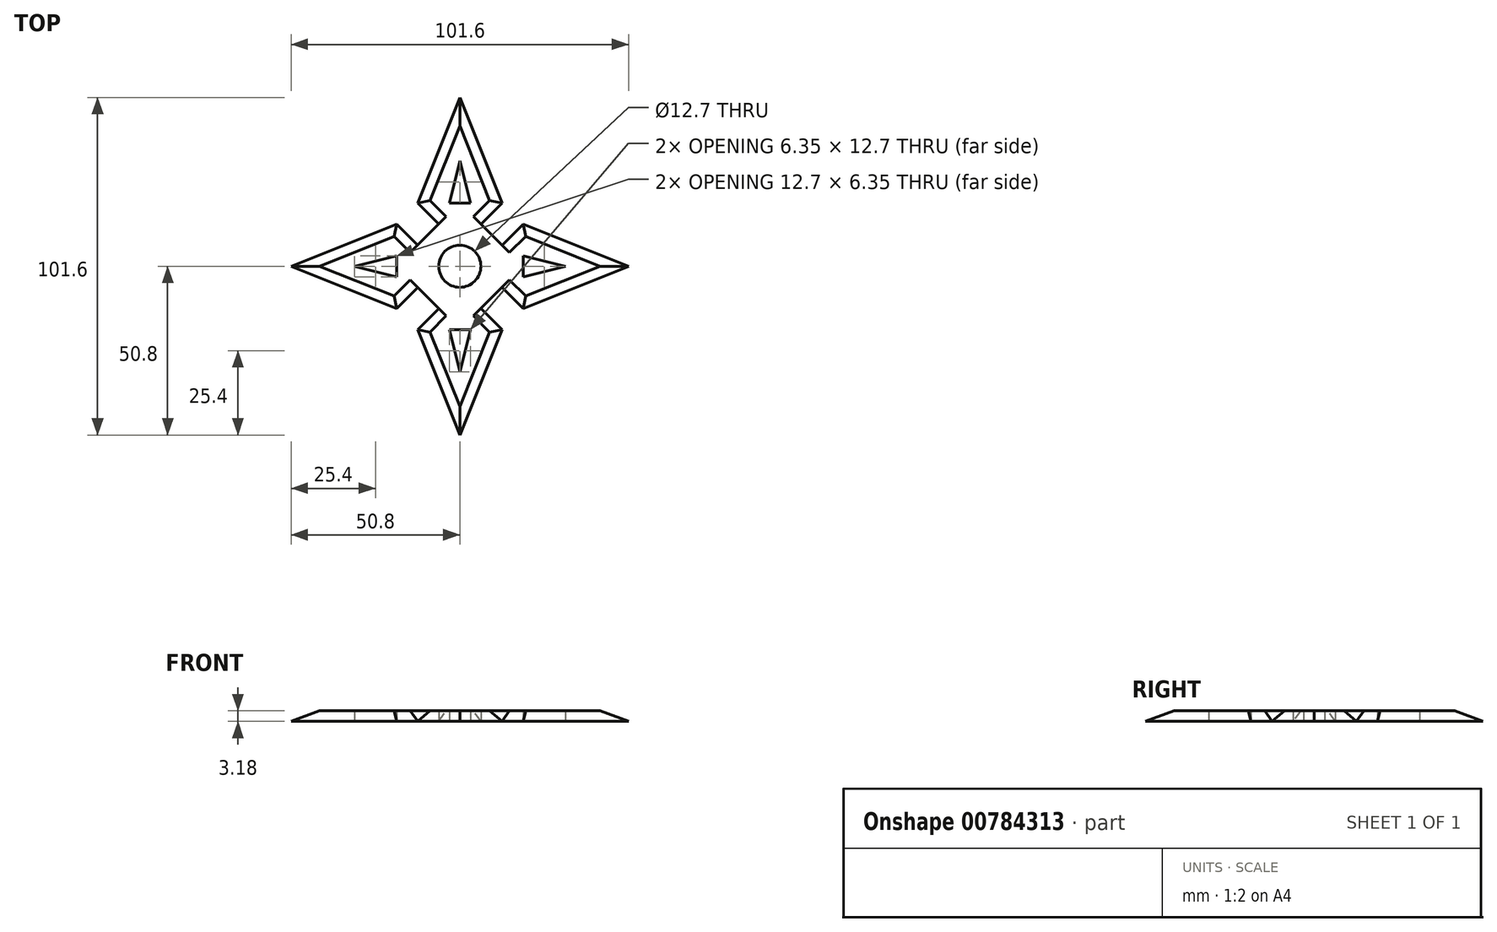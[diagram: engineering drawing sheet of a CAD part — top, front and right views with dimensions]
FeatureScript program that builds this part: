
annotation { "Feature Type Name" : "Feature", "Feature Type Description" : "" }
export const myFeature = defineFeature(function(context is Context, id is Id, definition is map)
    precondition{}
    {
        {
            var Q0;
            Q0=qCreatedBy(makeId("Top.planeOp"),FACE);
            var sketch = newSketch(context, id + "F0", { "sketchPlane" : qUnion([Q0])});
            skLineSegment(sketch, "E0", {"start": v(-12.7, 6.35) * mm, "end": v(-12.7, -6.35) * mm});
            skLineSegment(sketch, "E1", {"start": v(-12.7, -6.35) * mm, "end": v(-6.35, -12.7) * mm});
            skLineSegment(sketch, "E2", {"start": v(-6.35, -12.7) * mm, "end": v(6.35, -12.7) * mm});
            skLineSegment(sketch, "E3", {"start": v(6.35, -12.7) * mm, "end": v(12.7, -6.35) * mm});
            skLineSegment(sketch, "E4", {"start": v(12.7, -6.35) * mm, "end": v(12.7, 6.35) * mm});
            skLineSegment(sketch, "E5", {"start": v(12.7, 6.35) * mm, "end": v(6.35, 12.7) * mm});
            skLineSegment(sketch, "E6", {"start": v(6.35, 12.7) * mm, "end": v(-6.35, 12.7) * mm});
            skLineSegment(sketch, "E7", {"start": v(-6.35, 12.7) * mm, "end": v(-12.7, 6.35) * mm});
            skLineSegment(sketch, "E8", {"start": v(-6.35, 12.7) * mm, "end": v(-12.7, 19.05) * mm});
            skLineSegment(sketch, "E9", {"start": v(-12.7, 19.05) * mm, "end": v(0, 50.8) * mm});
            skLineSegment(sketch, "E10", {"start": v(0, 50.8) * mm, "end": v(12.7, 19.05) * mm});
            skLineSegment(sketch, "E11", {"start": v(12.7, 19.05) * mm, "end": v(6.35, 12.7) * mm});
            skLineSegment(sketch, "E12", {"start": v(0, 12.7) * mm, "end": v(0, 50.8) * mm, "construction": true});
            skLineSegment(sketch, "E13", {"start": v(0, 12.7) * mm, "end": v(0, -12.7) * mm, "construction": true});
            skLineSegment(sketch, "E14", {"start": v(-12.7, 0) * mm, "end": v(12.7, 0) * mm, "construction": true});
            skLineSegment(sketch, "E15.1.0", {"start": v(-12.7, 0) * mm, "end": v(-50.8, 0) * mm, "construction": true});
            skLineSegment(sketch, "E15.1.1", {"start": v(-50.8, 0) * mm, "end": v(-19.05, 12.7) * mm});
            skLineSegment(sketch, "E15.1.2", {"start": v(-19.05, -12.7) * mm, "end": v(-50.8, 0) * mm});
            skLineSegment(sketch, "E15.1.4", {"start": v(-19.05, 12.7) * mm, "end": v(-12.7, 6.35) * mm});
            skLineSegment(sketch, "E15.1.5", {"start": v(-12.7, -6.35) * mm, "end": v(-19.05, -12.7) * mm});
            skLineSegment(sketch, "E15.2.0", {"start": v(0, -12.7) * mm, "end": v(0, -50.8) * mm, "construction": true});
            skLineSegment(sketch, "E15.2.1", {"start": v(0, -50.8) * mm, "end": v(-12.7, -19.05) * mm});
            skLineSegment(sketch, "E15.2.2", {"start": v(12.7, -19.05) * mm, "end": v(0, -50.8) * mm});
            skLineSegment(sketch, "E15.2.4", {"start": v(-12.7, -19.05) * mm, "end": v(-6.35, -12.7) * mm});
            skLineSegment(sketch, "E15.2.5", {"start": v(6.35, -12.7) * mm, "end": v(12.7, -19.05) * mm});
            skLineSegment(sketch, "E15.2.6", {"start": v(0, -12.7) * mm, "end": v(0, 12.7) * mm, "construction": true});
            skLineSegment(sketch, "E15.3.0", {"start": v(12.7, 0) * mm, "end": v(50.8, 0) * mm, "construction": true});
            skLineSegment(sketch, "E15.3.1", {"start": v(50.8, 0) * mm, "end": v(19.05, -12.7) * mm});
            skLineSegment(sketch, "E15.3.2", {"start": v(19.05, 12.7) * mm, "end": v(50.8, 0) * mm});
            skLineSegment(sketch, "E15.3.4", {"start": v(19.05, -12.7) * mm, "end": v(12.7, -6.35) * mm});
            skLineSegment(sketch, "E15.3.5", {"start": v(12.7, 6.35) * mm, "end": v(19.05, 12.7) * mm});
            skLineSegment(sketch, "E15.3.6", {"start": v(12.7, 0) * mm, "end": v(-12.7, 0) * mm, "construction": true});
            skPoint(sketch, "E15.center", {"position": v(0, 0) * mm});
            skLineSegment(sketch, "E16", {"start": v(-3.18, 19.05) * mm, "end": v(0, 31.75) * mm});
            skLineSegment(sketch, "E17", {"start": v(0, 31.75) * mm, "end": v(3.17, 19.05) * mm});
            skLineSegment(sketch, "E18", {"start": v(-3.18, 19.05) * mm, "end": v(3.17, 19.05) * mm});
            skLineSegment(sketch, "E19.1.0", {"start": v(19.05, 3.18) * mm, "end": v(19.05, -3.17) * mm});
            skLineSegment(sketch, "E19.1.1", {"start": v(31.75, 0) * mm, "end": v(19.05, -3.17) * mm});
            skLineSegment(sketch, "E19.1.3", {"start": v(19.05, 3.18) * mm, "end": v(31.75, 0) * mm});
            skLineSegment(sketch, "E19.2.0", {"start": v(3.18, -19.05) * mm, "end": v(-3.17, -19.05) * mm});
            skLineSegment(sketch, "E19.2.1", {"start": v(0, -31.75) * mm, "end": v(-3.17, -19.05) * mm});
            skLineSegment(sketch, "E19.2.3", {"start": v(3.18, -19.05) * mm, "end": v(0, -31.75) * mm});
            skLineSegment(sketch, "E19.3.0", {"start": v(-19.05, -3.18) * mm, "end": v(-19.05, 3.17) * mm});
            skLineSegment(sketch, "E19.3.1", {"start": v(-31.75, 0) * mm, "end": v(-19.05, 3.17) * mm});
            skLineSegment(sketch, "E19.3.3", {"start": v(-19.05, -3.18) * mm, "end": v(-31.75, 0) * mm});
            skLineSegment(sketch, "E19.anchor1", {"start": v(0, 0) * mm, "end": v(0, 12.7) * mm, "construction": true});
            skLineSegment(sketch, "E19.anchor2", {"start": v(0, 0) * mm, "end": v(-12.7, 0) * mm, "construction": true});
            skCircle(sketch, "E20", {"center": v(0, 0) * mm, "radius": 6.35 * mm});
            skSolve(sketch);
        }
        {
            var Q0;
            Q0=makeQuery(id+"F0.imprint","IMPRINT",FACE,{"disambiguationData":[TD([[makeQuery(id+"F0.imprint","IMPRINT",EDGE,{"derivedFrom":sQuery(id+"F0.wireOp",EDGE,"E15.2.1")}),-1.0]])]});
            var Q1;
            Q1=makeQuery(id+"F0.imprint","IMPRINT",FACE,{"disambiguationData":[TD([[makeQuery(id+"F0.imprint","IMPRINT",EDGE,{"derivedFrom":sQuery(id+"F0.wireOp",EDGE,"E15.3.1")}),-1.0]])]});
            var Q2;
            Q2=makeQuery(id+"F0.imprint","IMPRINT",FACE,{"disambiguationData":[TD([[makeQuery(id+"F0.imprint","IMPRINT",EDGE,{"derivedFrom":sQuery(id+"F0.wireOp",EDGE,"E6")}),1.0]])]});
            var Q3;
            Q3=makeQuery(id+"F0.imprint","IMPRINT",FACE,{"disambiguationData":[TD([[makeQuery(id+"F0.imprint","IMPRINT",EDGE,{"derivedFrom":sQuery(id+"F0.wireOp",EDGE,"E15.1.1")}),-1.0]])]});
            var Q4;
            Q4=makeQuery(id+"F0.imprint","IMPRINT",FACE,{"disambiguationData":[TD([[makeQuery(id+"F0.imprint","IMPRINT",EDGE,{"derivedFrom":sQuery(id+"F0.wireOp",EDGE,"E6")}),-1.0]])]});
            extrude(context, id + "F1", {"entities" : qUnion([Q0, Q1, Q2, Q3, Q4]), "depth" : 3.17 * mm, "offsetDistance" : 25.4 * mm});
        }
        {
            var Q0;
            Q0=makeQuery(id+"F1.opExtrude","CAP_EDGE",EDGE,{"disambiguationData":[OSD([sQuery(id+"F0.wireOp",EDGE,"E15.2.2")])],"isStart":false});
            var Q1;
            Q1=makeQuery(id+"F1.opExtrude","CAP_EDGE",EDGE,{"disambiguationData":[OSD([sQuery(id+"F0.wireOp",EDGE,"E15.2.1")])],"isStart":false});
            var Q2;
            Q2=makeQuery(id+"F1.opExtrude","CAP_EDGE",EDGE,{"disambiguationData":[OSD([sQuery(id+"F0.wireOp",EDGE,"E15.2.4")])],"isStart":false});
            var Q3;
            Q3=makeQuery(id+"F1.opExtrude","CAP_EDGE",EDGE,{"disambiguationData":[OSD([sQuery(id+"F0.wireOp",EDGE,"E15.2.5")])],"isStart":false});
            var Q4;
            Q4=makeQuery(id+"F1.opExtrude","CAP_EDGE",EDGE,{"disambiguationData":[OSD([sQuery(id+"F0.wireOp",EDGE,"E15.3.1")])],"isStart":false});
            var Q5;
            Q5=makeQuery(id+"F1.opExtrude","CAP_EDGE",EDGE,{"disambiguationData":[OSD([sQuery(id+"F0.wireOp",EDGE,"E15.3.4")])],"isStart":false});
            var Q6;
            Q6=makeQuery(id+"F1.opExtrude","CAP_EDGE",EDGE,{"disambiguationData":[OSD([sQuery(id+"F0.wireOp",EDGE,"E15.3.2")])],"isStart":false});
            var Q7;
            Q7=makeQuery(id+"F1.opExtrude","CAP_EDGE",EDGE,{"disambiguationData":[OSD([sQuery(id+"F0.wireOp",EDGE,"E15.3.5")])],"isStart":false});
            var Q8;
            Q8=makeQuery(id+"F1.opExtrude","CAP_EDGE",EDGE,{"disambiguationData":[OSD([sQuery(id+"F0.wireOp",EDGE,"E3")])],"isStart":false});
            var Q9;
            Q9=makeQuery(id+"F1.opExtrude","CAP_EDGE",EDGE,{"disambiguationData":[OSD([sQuery(id+"F0.wireOp",EDGE,"E1")])],"isStart":false});
            var Q10;
            Q10=makeQuery(id+"F1.opExtrude","CAP_EDGE",EDGE,{"disambiguationData":[OSD([sQuery(id+"F0.wireOp",EDGE,"E15.1.5")])],"isStart":false});
            var Q11;
            Q11=makeQuery(id+"F1.opExtrude","CAP_EDGE",EDGE,{"disambiguationData":[OSD([sQuery(id+"F0.wireOp",EDGE,"E15.1.2")])],"isStart":false});
            var Q12;
            Q12=makeQuery(id+"F1.opExtrude","CAP_EDGE",EDGE,{"disambiguationData":[OSD([sQuery(id+"F0.wireOp",EDGE,"E15.1.1")])],"isStart":false});
            var Q13;
            Q13=makeQuery(id+"F1.opExtrude","CAP_EDGE",EDGE,{"disambiguationData":[OSD([sQuery(id+"F0.wireOp",EDGE,"E15.1.4")])],"isStart":false});
            var Q14;
            Q14=makeQuery(id+"F1.opExtrude","CAP_EDGE",EDGE,{"disambiguationData":[OSD([sQuery(id+"F0.wireOp",EDGE,"E7")])],"isStart":false});
            var Q15;
            Q15=makeQuery(id+"F1.opExtrude","CAP_EDGE",EDGE,{"disambiguationData":[OSD([sQuery(id+"F0.wireOp",EDGE,"E5")])],"isStart":false});
            var Q16;
            Q16=makeQuery(id+"F1.opExtrude","CAP_EDGE",EDGE,{"disambiguationData":[OSD([sQuery(id+"F0.wireOp",EDGE,"E8")])],"isStart":false});
            var Q17;
            Q17=makeQuery(id+"F1.opExtrude","CAP_EDGE",EDGE,{"disambiguationData":[OSD([sQuery(id+"F0.wireOp",EDGE,"E9")])],"isStart":false});
            var Q18;
            Q18=makeQuery(id+"F1.opExtrude","CAP_EDGE",EDGE,{"disambiguationData":[OSD([sQuery(id+"F0.wireOp",EDGE,"E10")])],"isStart":false});
            var Q19;
            Q19=makeQuery(id+"F1.opExtrude","CAP_EDGE",EDGE,{"disambiguationData":[OSD([sQuery(id+"F0.wireOp",EDGE,"E11")])],"isStart":false});
            chamfer(context, id + "F2", {"entities" : qUnion([Q0, Q1, Q2, Q3, Q4, Q5, Q6, Q7, Q8, Q9, Q10, Q11, Q12, Q13, Q14, Q15, Q16, Q17, Q18, Q19]), "width" : 3.17 * mm, "tangentPropagation" : true});
        }
    });
